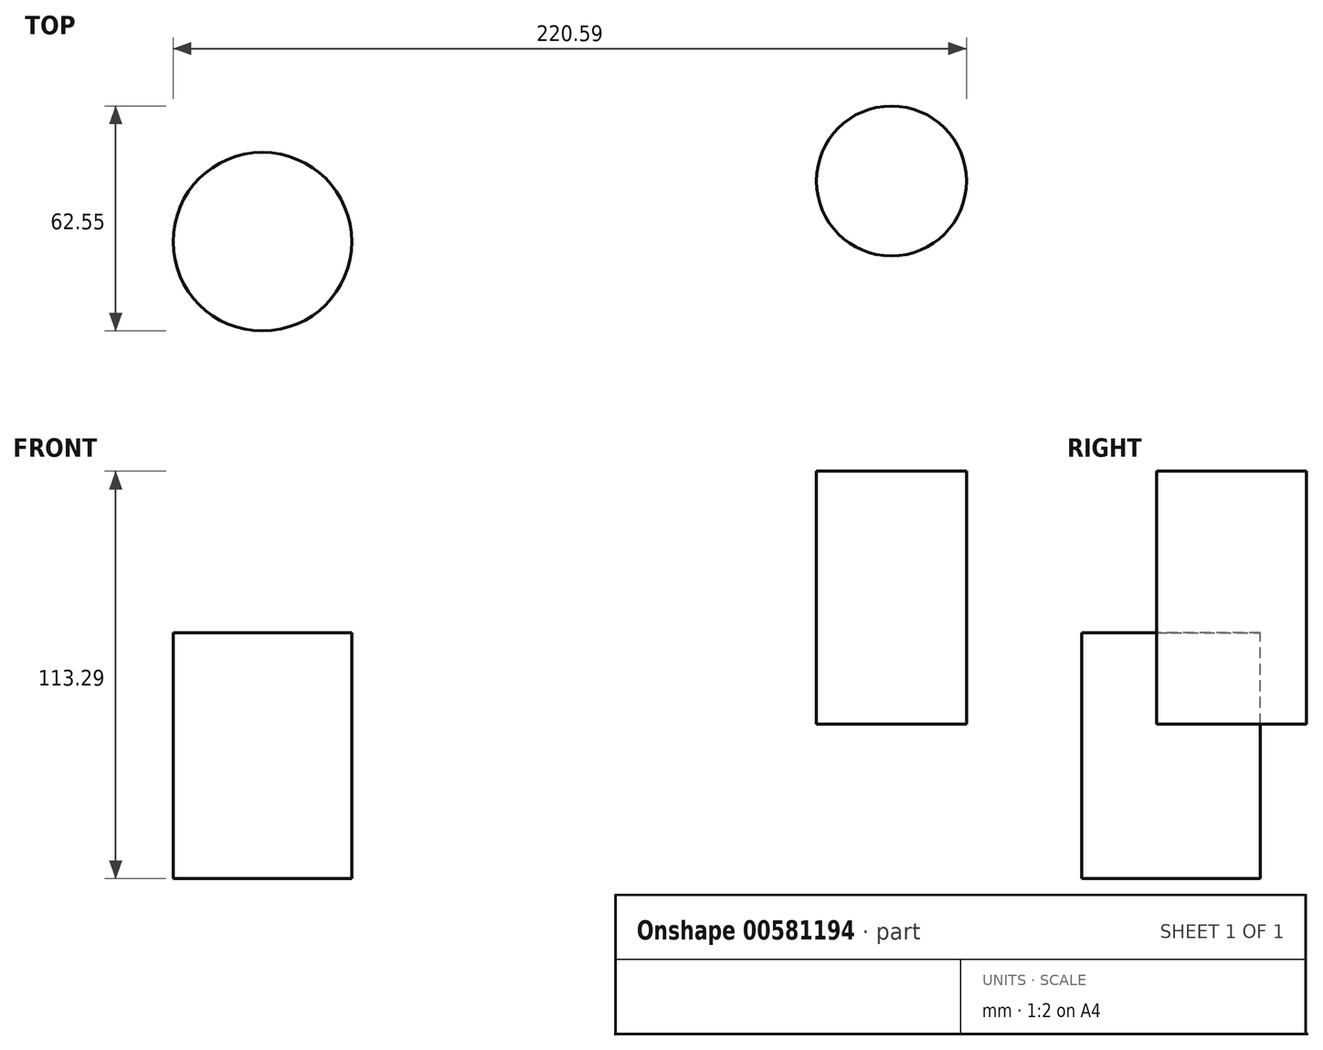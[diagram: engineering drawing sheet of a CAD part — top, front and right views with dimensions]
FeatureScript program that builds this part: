
annotation { "Feature Type Name" : "Feature", "Feature Type Description" : "" }
export const myFeature = defineFeature(function(context is Context, id is Id, definition is map)
    precondition{}
    {
        {
            var Q0;
            Q0=qCreatedBy(makeId("Top.planeOp"),FACE);
            var sketch = newSketch(context, id + "F0", { "sketchPlane" : qUnion([Q0])});
            skCircle(sketch, "E0", {"center": v(104.31, -43.01) * mm, "radius": 20.86 * mm});
            skCircle(sketch, "E1", {"center": v(99.86, -32.47) * mm, "radius": 39.78 * mm});
            skSolve(sketch);
        }
        {
            var Q0;
            Q0=makeQuery(id+"F0.imprint","IMPRINT",FACE,{"disambiguationData":[TD([[makeQuery(id+"F0.imprint","IMPRINT",EDGE,{"derivedFrom":sQuery(id+"F0.wireOp",EDGE,"E0")}),1.0]])]});
            extrude(context, id + "F1", {"entities" : qUnion([Q0]), "depth" : 70.36 * mm, "offsetDistance" : 25.4 * mm});
        }
        {
            var Q0;
            Q0=qCreatedBy(makeId("Top.planeOp"),FACE);
            var sketch = newSketch(context, id + "F2", { "sketchPlane" : qUnion([Q0])});
            skCircle(sketch, "E2", {"center": v(-70.58, -59.87) * mm, "radius": 24.83 * mm});
            skSolve(sketch);
        }
        {
            var Q0;
            Q0=makeQuery(id+"F2.imprint","IMPRINT",FACE,{"disambiguationData":[TD([[makeQuery(id+"F2.imprint","IMPRINT",EDGE,{"derivedFrom":sQuery(id+"F2.wireOp",EDGE,"E2")}),1.0]])]});
            extrude(context, id + "F3", {"entities" : qUnion([Q0]), "oppositeDirection" : true, "depth" : 42.93 * mm, "offsetDistance" : 25.4 * mm});
        }
        {
            var Q0;
            Q0=makeQuery(id+"F3.opExtrude","CAP_FACE",FACE,{"disambiguationData":[OSD([sQuery(id+"F2.wireOp",EDGE,"E2")])],"isStart":true});
            extrude(context, id + "F4", {"entities" : qUnion([Q0]), "operationType" : NewBodyOperationType.ADD, "depth" : 25.4 * mm, "offsetDistance" : 25.4 * mm});
        }
    });
